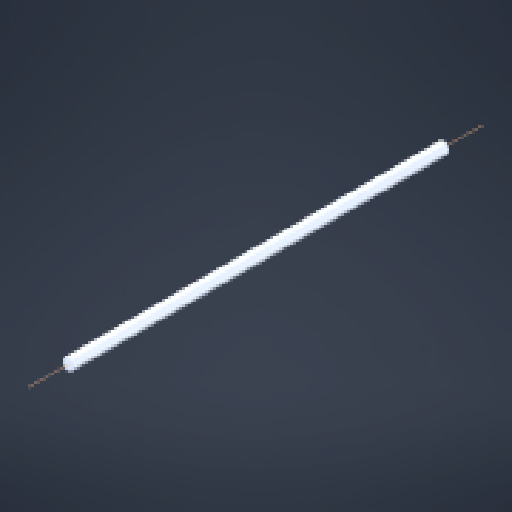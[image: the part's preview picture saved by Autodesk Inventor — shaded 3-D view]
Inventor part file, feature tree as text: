
AUTODESK INVENTOR PART (.ipt)
format: ipt  version: 2024 (Build 280153000, 153)  size: 203,776 bytes
history: native  units: in
note: dims shown in document units (in); Inventor stores cm internally (conversion verified against a paired STEP export)
features: sketch x1, other x1, fillet x1
ambient origin geometry x8: Origin, YZ Plane, XZ Plane, XY Plane, X Axis, Y Axis, Z Axis, Center Point
bodies: Solid1 (feature_tree)
feature tree (3):
  sketch  "Sketch1"
  other  "Work Axis1"
  fillet  "Fillet1"  [1 undecoded]
note: 1 required parameter value undecoded (feature->parameter linkage not recoverable at this tier; creation-order binding heuristic only, values carry confidence <= 0.55)
